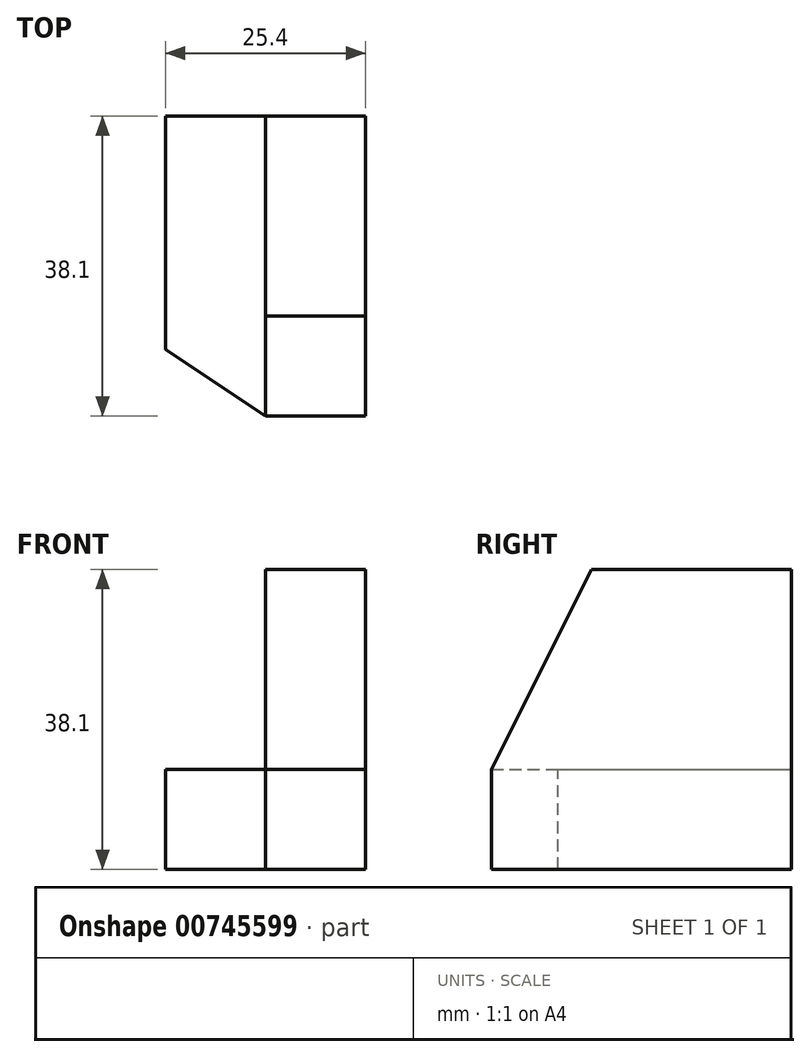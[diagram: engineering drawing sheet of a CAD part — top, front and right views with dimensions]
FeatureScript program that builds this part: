
annotation { "Feature Type Name" : "Feature", "Feature Type Description" : "" }
export const myFeature = defineFeature(function(context is Context, id is Id, definition is map)
    precondition{}
    {
        {
            var Q0;
            Q0=qCreatedBy(makeId("Front.planeOp"),FACE);
            var sketch = newSketch(context, id + "F0", { "sketchPlane" : qUnion([Q0])});
            skLineSegment(sketch, "E0", {"start": v(0, 0) * mm, "end": v(25.4, 0) * mm});
            skLineSegment(sketch, "E1", {"start": v(25.4, 0) * mm, "end": v(25.4, 38.1) * mm});
            skLineSegment(sketch, "E2", {"start": v(25.4, 38.1) * mm, "end": v(12.7, 38.1) * mm});
            skLineSegment(sketch, "E3", {"start": v(12.7, 38.1) * mm, "end": v(12.7, 12.7) * mm});
            skLineSegment(sketch, "E4", {"start": v(12.7, 12.7) * mm, "end": v(0, 12.7) * mm});
            skLineSegment(sketch, "E5", {"start": v(0, 12.7) * mm, "end": v(0, 0) * mm});
            skSolve(sketch);
        }
        {
            var Q0;
            Q0=makeQuery(id+"F0.imprint","IMPRINT",FACE,{"disambiguationData":[TD([[makeQuery(id+"F0.imprint","IMPRINT",EDGE,{"derivedFrom":sQuery(id+"F0.wireOp",EDGE,"E0")}),1.0]])]});
            extrude(context, id + "F1", {"entities" : qUnion([Q0]), "depth" : 38.1 * mm, "offsetDistance" : 25.4 * mm});
        }
        {
            var Q0;
            Q0=makeQuery(id+"F1.opExtrude","SWEPT_FACE",FACE,{"disambiguationData":[OSD([sQuery(id+"F0.wireOp",EDGE,"E3")])]});
            var sketch = newSketch(context, id + "F2", { "sketchPlane" : qUnion([Q0])});
            skLineSegment(sketch, "E6", {"start": v(25.4, 38.1) * mm, "end": v(38.1, 12.7) * mm});
            skLineSegment(sketch, "E7", {"start": v(38.1, 12.7) * mm, "end": v(38.1, 38.1) * mm});
            skLineSegment(sketch, "E8", {"start": v(38.1, 38.1) * mm, "end": v(25.4, 38.1) * mm});
            skSolve(sketch);
        }
        {
            var Q0;
            Q0=makeQuery(id+"F2.imprint","IMPRINT",FACE,{"disambiguationData":[TD([[makeQuery(id+"F2.imprint","IMPRINT",EDGE,{"derivedFrom":sQuery(id+"F2.wireOp",EDGE,"E6")}),1.0]])]});
            extrude(context, id + "F3", {"entities" : qUnion([Q0]), "operationType" : NewBodyOperationType.REMOVE, "oppositeDirection" : true, "depth" : 12.7 * mm, "offsetDistance" : 25.4 * mm});
        }
        {
            var Q0;
            Q0=makeQuery(id+"F1.opExtrude","SWEPT_FACE",FACE,{"disambiguationData":[OSD([sQuery(id+"F0.wireOp",EDGE,"E4")])]});
            var sketch = newSketch(context, id + "F4", { "sketchPlane" : qUnion([Q0])});
            skLineSegment(sketch, "E9", {"start": v(12.7, -38.1) * mm, "end": v(0, -31.63) * mm});
            skLineSegment(sketch, "E10", {"start": v(0, -31.63) * mm, "end": v(-12.7, -31.63) * mm});
            skLineSegment(sketch, "E11", {"start": v(-12.7, -31.63) * mm, "end": v(-12.7, -38.1) * mm});
            skLineSegment(sketch, "E12", {"start": v(-12.7, -38.1) * mm, "end": v(12.7, -38.1) * mm});
            skSolve(sketch);
        }
        {
            var Q0;
            {var subQ0=sQuery(id+"F4.wireOp",EDGE,"E9");Q0=makeQuery(id+"F4.imprint","IMPRINT",FACE,{"disambiguationData":[TD([[makeQuery(id+"F4.imprint","IMPRINT",EDGE,{"derivedFrom":subQ0}),1.0]])]});}
            extrude(context, id + "F5", {"entities" : qUnion([Q0]), "operationType" : NewBodyOperationType.ADD, "depth" : 12.7 * mm, "offsetDistance" : 25.4 * mm});
        }
        {
            var Q0;
            Q0=makeQuery(id+"F5.opExtrude","SWEPT_FACE",FACE,{"disambiguationData":[OSD([sQuery(id+"F4.wireOp",EDGE,"E9")])]});
            extrude(context, id + "F6", {"entities" : qUnion([Q0]), "operationType" : NewBodyOperationType.REMOVE, "oppositeDirection" : true, "depth" : 25.4 * mm, "offsetDistance" : 25.4 * mm});
        }
        {
            var Q0;
            {var subQ0=sQuery(id+"F4.wireOp",EDGE,"E9");Q0=makeQuery(id+"F6.boolean.opBoolean","MERGE",FACE,{"derivedFrom":[makeQuery(id+"F1.opExtrude","SWEPT_FACE",FACE,{"disambiguationData":[OSD([sQuery(id+"F0.wireOp",EDGE,"E4")])]}),makeQuery(id+"F6.opExtrude","SWEPT_FACE",FACE,{"disambiguationData":[OSD([subQ0]),TDD([makeQuery(id+"F5.opExtrude","CAP_EDGE",EDGE,{"disambiguationData":[OSD([subQ0])],"isStart":true})])]})]});}
            var sketch = newSketch(context, id + "F7", { "sketchPlane" : qUnion([Q0])});
            skLineSegment(sketch, "E13", {"start": v(0, -29.64) * mm, "end": v(0, -38.1) * mm});
            skLineSegment(sketch, "E14", {"start": v(0, -38.1) * mm, "end": v(12.7, -38.1) * mm});
            skLineSegment(sketch, "E15", {"start": v(12.7, -38.1) * mm, "end": v(0, -29.64) * mm});
            skSolve(sketch);
        }
        {
            var Q0;
            Q0=makeQuery(id+"F7.imprint","IMPRINT",FACE,{"disambiguationData":[TD([[makeQuery(id+"F7.imprint","IMPRINT",EDGE,{"derivedFrom":sQuery(id+"F7.wireOp",EDGE,"E13")}),-1.0]])]});
            extrude(context, id + "F8", {"entities" : qUnion([Q0]), "operationType" : NewBodyOperationType.REMOVE, "oppositeDirection" : true, "depth" : 12.7 * mm, "offsetDistance" : 25.4 * mm});
        }
    });
